# Revit family: SNS Merlin 1000V+ Gas Pressure Proving
name_source: partatom
category: Electrical Equipment
units: mm (PartAtom-declared; Revit-internal decimal feet)

## family parameters
Always vertical = Yes
Cut with Voids When Loaded = No
OmniClass Number = 23.80.30.11.17
OmniClass Title = Distribution Boards and Control Panels
Part Type = Other Panel
Room Calculation Point = No
Round Connector Dimension = Use Diameter
Shared = No
Work Plane-Based = No

## types (1)
- AGS Merlin 1000V+
    Default Height = 4' - 0"
    Description = The Merlin 1000V+ Laboratory Utility Controller is designed specifically for use in School and University Laboratories. This panel is to be used to carry out a gas proving test on the pipe work in order to highlight if there is a gas appliance open or a gas leak in the laboratory. The Merlin 1000V+ is designed to give the teacher full control over the incoming gas supply and bench electrics with the lockable main key-switch and touch sensors.

The Merlin 1000V+ can work in conjunction with carbon dioxide, natural gas, carbon monoxide and LPG sensors. The Merlin 1000V+ also has a built in “timeout” facility which will automatically shut off the gas solenoid valve at the end of a specific time period, this time period can be adjusted to 2, 4, 8 hours or can be overridden if required.
    Load = 120 VA
    Manufacturer = S&S Northern Ltd.
    Model = SNS Merlin 1000V+
    Product Information = http://snsnorthern.com
    Type Comments = Merlin 1000V+ incl. Gas Pressure Proving Transducer protection.
    URL = http://snsnorthern.com
    Voltage = 120VAC

## geometry (parser evidence)
native form markers: Sweep x15
no freeform markers — native parametric forms only
